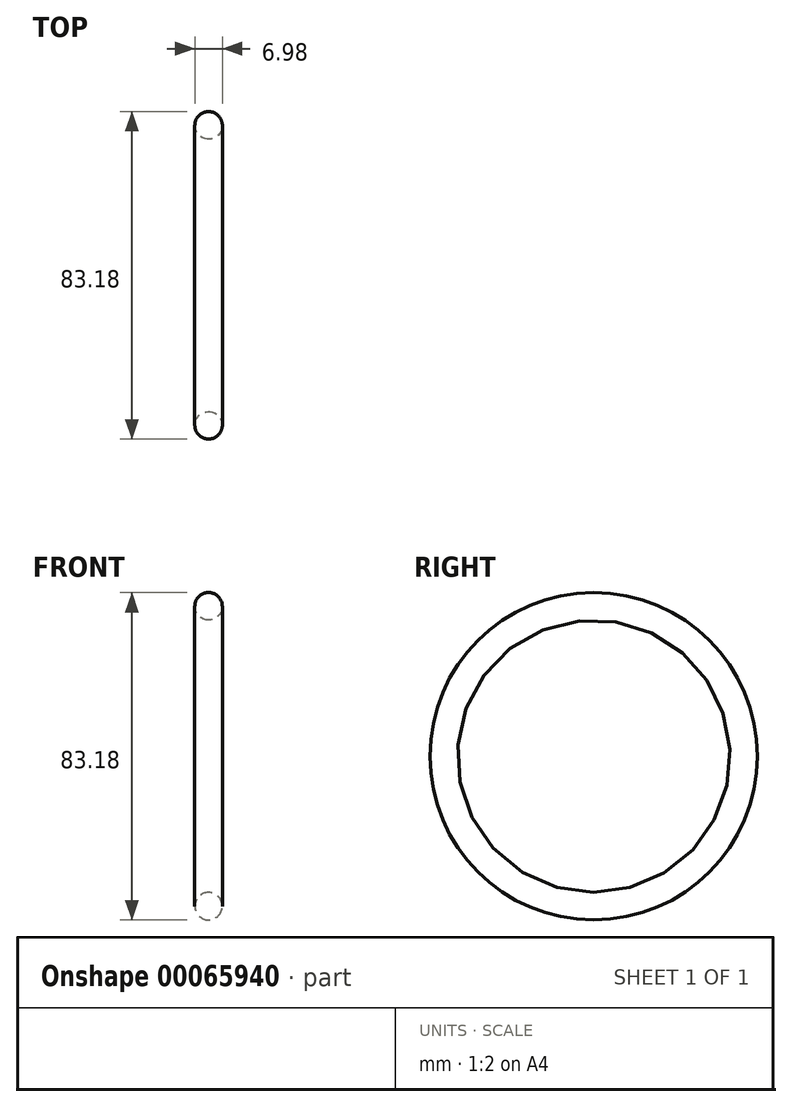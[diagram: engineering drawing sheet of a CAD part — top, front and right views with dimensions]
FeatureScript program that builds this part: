
annotation { "Feature Type Name" : "Feature", "Feature Type Description" : "" }
export const myFeature = defineFeature(function(context is Context, id is Id, definition is map)
    precondition{}
    {
        {
            var Q0;
            Q0=qCreatedBy(makeId("Front.planeOp"),FACE);
            var sketch = newSketch(context, id + "F0", { "sketchPlane" : qUnion([Q0])});
            skLineSegment(sketch, "E0", {"start": v(0, 0) * mm, "end": v(-6.06, 0) * mm, "construction": true});
            skCircle(sketch, "E1", {"center": v(0, 38.1) * mm, "radius": 3.5 * mm});
            skSolve(sketch);
        }
        {
            var Q0;
            Q0=makeQuery(id+"F0.imprint","IMPRINT",FACE,{"disambiguationData":[TD([[makeQuery(id+"F0.imprint","IMPRINT",EDGE,{"derivedFrom":sQuery(id+"F0.wireOp",EDGE,"E1")}),1.0]])]});
            var Q1;
            Q1=sQuery(id+"F0.wireOp",EDGE,"E0");
            revolve(context, id + "F1", {"entities" : qUnion([Q0]), "axis" : qUnion([Q1]), "revolveType" : RevolveType.FULL});
        }
    });
